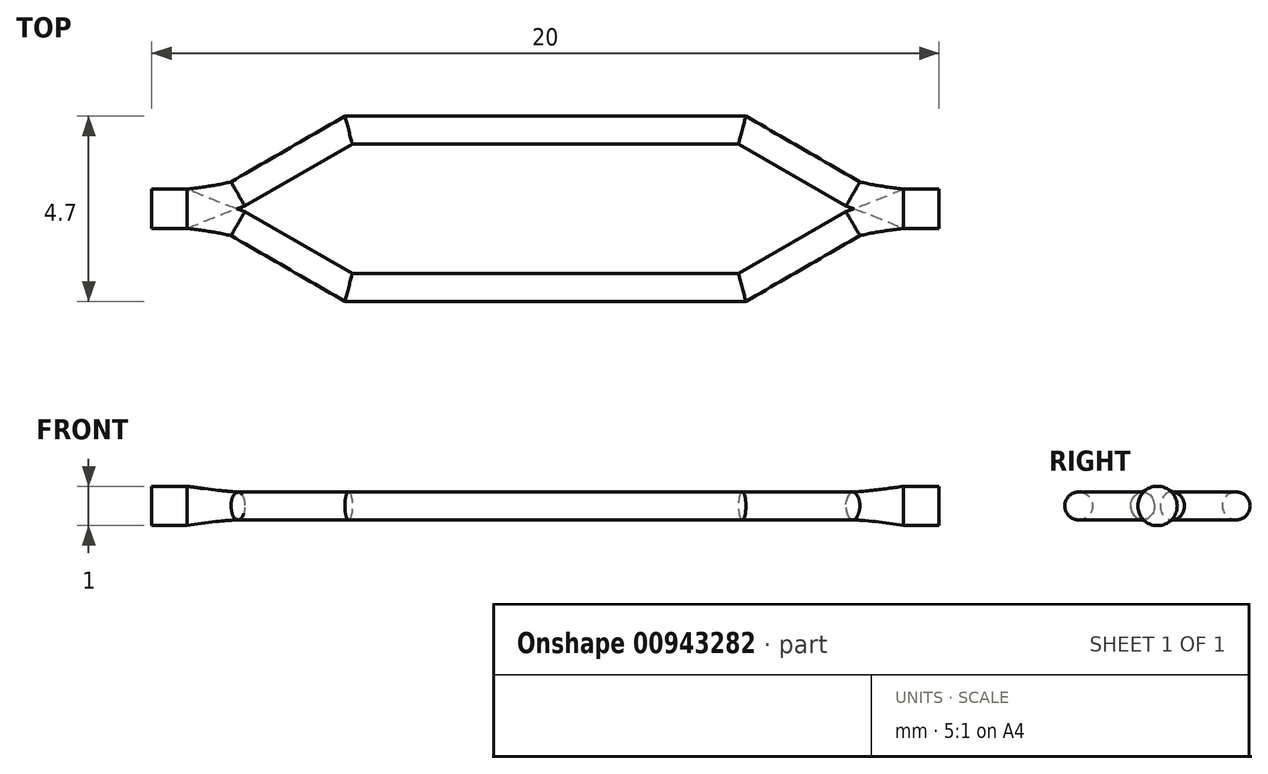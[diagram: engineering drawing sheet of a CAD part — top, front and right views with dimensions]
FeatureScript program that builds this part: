
annotation { "Feature Type Name" : "Feature", "Feature Type Description" : "" }
export const myFeature = defineFeature(function(context is Context, id is Id, definition is map)
    precondition{}
    {
        {
            var Q0;
            Q0=qCreatedBy(makeId("Top.planeOp"),FACE);
            var sketch = newSketch(context, id + "F0", { "sketchPlane" : qUnion([Q0])});
            skLineSegment(sketch, "E0.bottom", {"start": v(0, 7) * mm, "end": v(20, 7) * mm});
            skLineSegment(sketch, "E0.top", {"start": v(0, 0) * mm, "end": v(20, 0) * mm});
            skLineSegment(sketch, "E0.left", {"start": v(0, 7) * mm, "end": v(0, 0) * mm});
            skLineSegment(sketch, "E0.right", {"start": v(20, 7) * mm, "end": v(20, 0) * mm});
            skLineSegment(sketch, "E1", {"start": v(0, 3.5) * mm, "end": v(20, 3.5) * mm});
            skLineSegment(sketch, "E2", {"start": v(10, 7) * mm, "end": v(10, 0) * mm});
            skLineSegment(sketch, "E3", {"start": v(0, 3.5) * mm, "end": v(1.54, 3.5) * mm});
            skLineSegment(sketch, "E4", {"start": v(1.54, 3.5) * mm, "end": v(5, 5.5) * mm});
            skLineSegment(sketch, "E5", {"start": v(5, 5.5) * mm, "end": v(10, 5.5) * mm});
            skLineSegment(sketch, "E6", {"start": v(0, 3.5) * mm, "end": v(0.9, 3.5) * mm});
            skPoint(sketch, "E7", {"position": v(2.19, 3.88) * mm});
            skLineSegment(sketch, "E8", {"start": v(1.54, 3.5) * mm, "end": v(2.19, 3.88) * mm});
            skLineSegment(sketch, "E9", {"start": v(2.19, 3.88) * mm, "end": v(5, 5.5) * mm});
            skSolve(sketch);
        }
        {
            var Q0;
            Q0=qCreatedBy(makeId("Right.planeOp"),FACE);
            var sketch = newSketch(context, id + "F1", { "sketchPlane" : qUnion([Q0])});
            skCircle(sketch, "E10", {"center": v(3.5, 0) * mm, "radius": 0.5 * mm});
            skSolve(sketch);
        }
        {
            var Q0;
            Q0=makeQuery(id+"F1.imprint","IMPRINT",FACE,{"disambiguationData":[TD([[makeQuery(id+"F1.imprint","IMPRINT",EDGE,{"derivedFrom":sQuery(id+"F1.wireOp",EDGE,"E10")}),1.0]])]});
            var Q1;
            Q1=qSketchRegion(id+"FpUvRAgT4jxrOPf_1",true);
            var Q2;
            Q2=sQuery(id+"F0.wireOp",EDGE,"E6");
            sweep(context, id + "F2", {"profiles" : qUnion([Q0, Q1]), "path" : qUnion([Q2])});
        }
        {
            var Q0;
            Q0=sQuery(id+"F0.wireOp",EDGE,"E2");
            cPoint(context, id + "F3", {"entities" : qUnion([Q0]), "parameter" : 0.5});
        }
        {
            var Q0;
            Q0=sQuery(id+"F0.wireOp",EDGE,"E2");
            var Q1;
            Q1=qCreatedBy(id+"F3",VERTEX);
            cPlane(context, id + "F4", {"entities" : qUnion([Q0, Q1]), "cplaneType" : CPlaneType.LINE_POINT, "offset" : 25 * mm, "width" : 150 * mm, "height" : 150 * mm});
        }
        {
            var Q0;
            Q0=sQuery(id+"F0.wireOp",EDGE,"E0.bottom");
            cPoint(context, id + "F5", {"entities" : qUnion([Q0]), "parameter" : 0.5});
        }
        {
            var Q0;
            Q0=sQuery(id+"F0.wireOp",EDGE,"E0.bottom");
            var Q1;
            Q1=qCreatedBy(id+"F5",VERTEX);
            cPlane(context, id + "F6", {"entities" : qUnion([Q0, Q1]), "cplaneType" : CPlaneType.LINE_POINT, "offset" : 25 * mm, "width" : 150 * mm, "height" : 150 * mm});
        }
        {
            var Q0;
            Q0=sQuery(id+"F0.wireOp",EDGE,"E4");
            var Q1;
            Q1=sQuery(id+"F0.wireOp",VERTEX,"E7");
            var Q2;
            Q2=qBodyType(qCreatedBy(id+"F8",EDGE),BodyType.WIRE);
            cPlane(context, id + "F7", {"entities" : qUnion([Q0, Q1, Q2]), "cplaneType" : CPlaneType.LINE_POINT, "offset" : 25 * mm, "width" : 150 * mm, "height" : 150 * mm});
        }
        {
            var Q0;
            Q0=qCreatedBy(id+"F7.planeOp",FACE);
            var sketch = newSketch(context, id + "F8", { "sketchPlane" : qUnion([Q0])});
            skCircle(sketch, "E11", {"center": v(2.26, 0) * mm, "radius": 0.35 * mm});
            skSolve(sketch);
        }
        {
            var Q0;
            Q0=makeQuery(id+"F8.imprint","IMPRINT",FACE,{"disambiguationData":[TD([[makeQuery(id+"F8.imprint","IMPRINT",EDGE,{"derivedFrom":sQuery(id+"F8.wireOp",EDGE,"E11")}),1.0]])]});
            var Q1;
            Q1=sQuery(id+"F0.wireOp",EDGE,"E9");
            var Q2;
            Q2=sQuery(id+"F0.wireOp",EDGE,"E5");
            sweep(context, id + "F9", {"profiles" : qUnion([Q0]), "path" : qUnion([Q1, Q2])});
        }
        {
            var Q0;
            Q0=makeQuery(id+"F2.opSweep","CAP_FACE",FACE,{"disambiguationData":[OSD([sQuery(id+"F0.wireOp",VERTEX,"E6.end"),sQuery(id+"F1.wireOp",EDGE,"E10")])],"isStart":false});
            var Q1;
            Q1=makeQuery(id+"F9.opSweep","CAP_FACE",FACE,{"disambiguationData":[OSD([sQuery(id+"F0.wireOp",VERTEX,"E9.start"),sQuery(id+"F8.wireOp",EDGE,"E11")])],"isStart":true});
            var Q2;
            Q2=makeQuery(id+"F2.opSweep","CAP_FACE",FACE,{"disambiguationData":[OSD([sQuery(id+"F0.wireOp",VERTEX,"E6.end"),sQuery(id+"F1.wireOp",EDGE,"E10")])],"isStart":false});
            var Q3;
            Q3=makeQuery(id+"F9.opSweep","CAP_FACE",FACE,{"disambiguationData":[OSD([sQuery(id+"F0.wireOp",VERTEX,"E9.start"),sQuery(id+"F8.wireOp",EDGE,"E11")])],"isStart":true});
            var Q4;
            Q4=sQuery(id+"F0.wireOp",VERTEX,"E6.end");
            var Q5;
            Q5=sQuery(id+"F0.wireOp",VERTEX,"E7");
            loft(context, id + "F10", {"sheetProfilesArray" : [{ "sheetProfileEntities" : qUnion([Q0]) }, { "sheetProfileEntities" : qUnion([Q1]) }], "wireProfilesArray" : [{ "wireProfileEntities" : qUnion([Q2]) }, { "wireProfileEntities" : qUnion([Q3]) }], "connections" : [{ "connectionEntities" : qUnion([Q4, Q5]), "connectionEdgeQueries" : qUnion([]), "connectionEdgeParameters" : [] }]});
        }
        {
            var Q0;
            Q0=makeQuery(id+"F2.opSweep","SWEPT_BODY",BODY,{"disambiguationData":[OSD([sQuery(id+"F0.wireOp",EDGE,"E6"),sQuery(id+"F1.wireOp",EDGE,"E10")])]});
            var Q1;
            Q1=makeQuery(id+"F10.opLoft","SWEPT_BODY",BODY,{"disambiguationData":[OSD([sQuery(id+"F0.wireOp",VERTEX,"E6.end"),sQuery(id+"F0.wireOp",VERTEX,"E9.start"),sQuery(id+"F1.wireOp",EDGE,"E10"),sQuery(id+"F8.wireOp",EDGE,"E11")])]});
            var Q2;
            Q2=makeQuery(id+"F9.opSweep","SWEPT_BODY",BODY,{"disambiguationData":[OSD([sQuery(id+"F0.wireOp",EDGE,"E5"),sQuery(id+"F8.wireOp",EDGE,"E11")])]});
            var Q3;
            Q3=qCreatedBy(id+"F6.planeOp",FACE);
            mirror(context, id + "F11", {"operationType" : NewBodyOperationType.ADD, "entities" : qUnion([Q0, Q1, Q2]), "mirrorPlane" : qUnion([Q3])});
        }
        {
            var Q0;
            Q0=makeQuery(id+"F2.opSweep","SWEPT_BODY",BODY,{"disambiguationData":[OSD([sQuery(id+"F0.wireOp",EDGE,"E6"),sQuery(id+"F1.wireOp",EDGE,"E10")])]});
            var Q1;
            Q1=makeQuery(id+"F10.opLoft","SWEPT_BODY",BODY,{"disambiguationData":[OSD([sQuery(id+"F0.wireOp",VERTEX,"E6.end"),sQuery(id+"F0.wireOp",VERTEX,"E9.start"),sQuery(id+"F1.wireOp",EDGE,"E10"),sQuery(id+"F8.wireOp",EDGE,"E11")])]});
            var Q2;
            Q2=makeQuery(id+"F9.opSweep","SWEPT_BODY",BODY,{"disambiguationData":[OSD([sQuery(id+"F0.wireOp",EDGE,"E5"),sQuery(id+"F8.wireOp",EDGE,"E11")])]});
            var Q3;
            Q3=qCreatedBy(id+"F4.planeOp",FACE);
            mirror(context, id + "F12", {"entities" : qUnion([Q0, Q1, Q2]), "mirrorPlane" : qUnion([Q3])});
        }
    });
